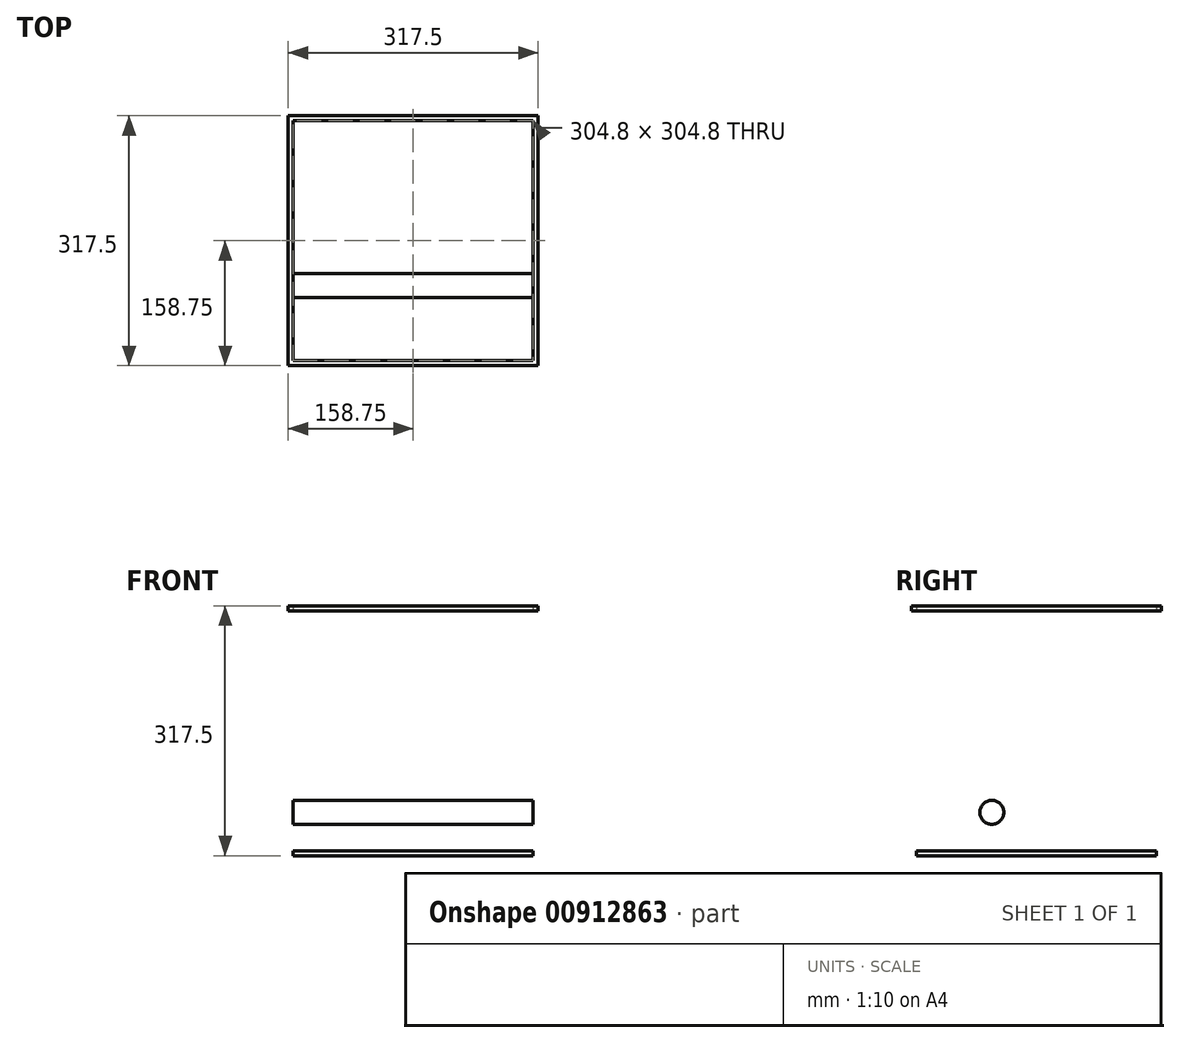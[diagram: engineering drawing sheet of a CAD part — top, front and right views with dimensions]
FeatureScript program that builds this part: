
annotation { "Feature Type Name" : "Feature", "Feature Type Description" : "" }
export const myFeature = defineFeature(function(context is Context, id is Id, definition is map)
    precondition{}
    {
        {
            var Q0;
            Q0=qCreatedBy(makeId("Top.planeOp"),FACE);
            var sketch = newSketch(context, id + "F0", { "sketchPlane" : qUnion([Q0])});
            skLineSegment(sketch, "E0.bottom", {"start": v(152.4, -152.4) * mm, "end": v(-152.4, -152.4) * mm});
            skLineSegment(sketch, "E0.top", {"start": v(152.4, 152.4) * mm, "end": v(-152.4, 152.4) * mm});
            skLineSegment(sketch, "E0.left", {"start": v(152.4, -152.4) * mm, "end": v(152.4, 152.4) * mm});
            skLineSegment(sketch, "E0.right", {"start": v(-152.4, -152.4) * mm, "end": v(-152.4, 152.4) * mm});
            skPoint(sketch, "E0.middle", {"position": v(0, 0) * mm});
            skSolve(sketch);
        }
        {
            var Q0;
            Q0 = qSketchRegion(id + "F0", true);
            extrude(context, id + "F1", {"entities" : qUnion([Q0]), "oppositeDirection" : true, "depth" : 6.35 * mm, "offsetDistance" : 25.4 * mm});
        }
        {
            var Q0;
            Q0=qCreatedBy(makeId("Top.planeOp"),FACE);
            cPlane(context, id + "F2", {"entities" : qUnion([Q0]), "cplaneType" : CPlaneType.OFFSET, "offset" : 304.8 * mm, "width" : 152.4 * mm, "height" : 152.4 * mm});
        }
        {
            var Q0;
            Q0=qCreatedBy(id+"F2.planeOp",FACE);
            var sketch = newSketch(context, id + "F3", { "sketchPlane" : qUnion([Q0])});
            skLineSegment(sketch, "E1.0", {"start": v(152.4, 152.4) * mm, "end": v(-152.4, 152.4) * mm});
            skLineSegment(sketch, "E1.1", {"start": v(-152.4, -152.4) * mm, "end": v(-152.4, 152.4) * mm});
            skLineSegment(sketch, "E1.2", {"start": v(152.4, -152.4) * mm, "end": v(152.4, 152.4) * mm});
            skLineSegment(sketch, "E1.3", {"start": v(152.4, -152.4) * mm, "end": v(-152.4, -152.4) * mm});
            skLineSegment(sketch, "E2.0", {"start": v(158.75, -158.75) * mm, "end": v(-158.75, -158.75) * mm});
            skLineSegment(sketch, "E2.1", {"start": v(158.75, -158.75) * mm, "end": v(158.75, 158.75) * mm});
            skLineSegment(sketch, "E2.2", {"start": v(158.75, 158.75) * mm, "end": v(-158.75, 158.75) * mm});
            skLineSegment(sketch, "E2.3", {"start": v(-158.75, -158.75) * mm, "end": v(-158.75, 158.75) * mm});
            skSolve(sketch);
        }
        {
            var Q0;
            Q0 = qSketchRegion(id + "F3", true);
            extrude(context, id + "F4", {"entities" : qUnion([Q0]), "depth" : 6.35 * mm, "offsetDistance" : 25.4 * mm});
        }
        {
            var Q0;
            Q0=qCreatedBy(makeId("Right.planeOp"),FACE);
            var sketch = newSketch(context, id + "F5", { "sketchPlane" : qUnion([Q0])});
            skCircle(sketch, "E3", {"center": v(-56.72, 48.72) * mm, "radius": 15.24 * mm});
            skSolve(sketch);
        }
        {
            var Q0;
            Q0=makeQuery(id+"F5.imprint","IMPRINT",FACE,{"disambiguationData":[TD([[makeQuery(id+"F5.imprint","IMPRINT",EDGE,{"derivedFrom":sQuery(id+"F5.wireOp",EDGE,"E3")}),1.0]])]});
            extrude(context, id + "F6", {"entities" : qUnion([Q0]), "depth" : 152.4 * mm, "offsetDistance" : 25.4 * mm, "hasSecondDirection" : true, "secondDirectionOppositeDirection" : true, "secondDirectionDepth" : 152.4 * mm});
        }
    });
